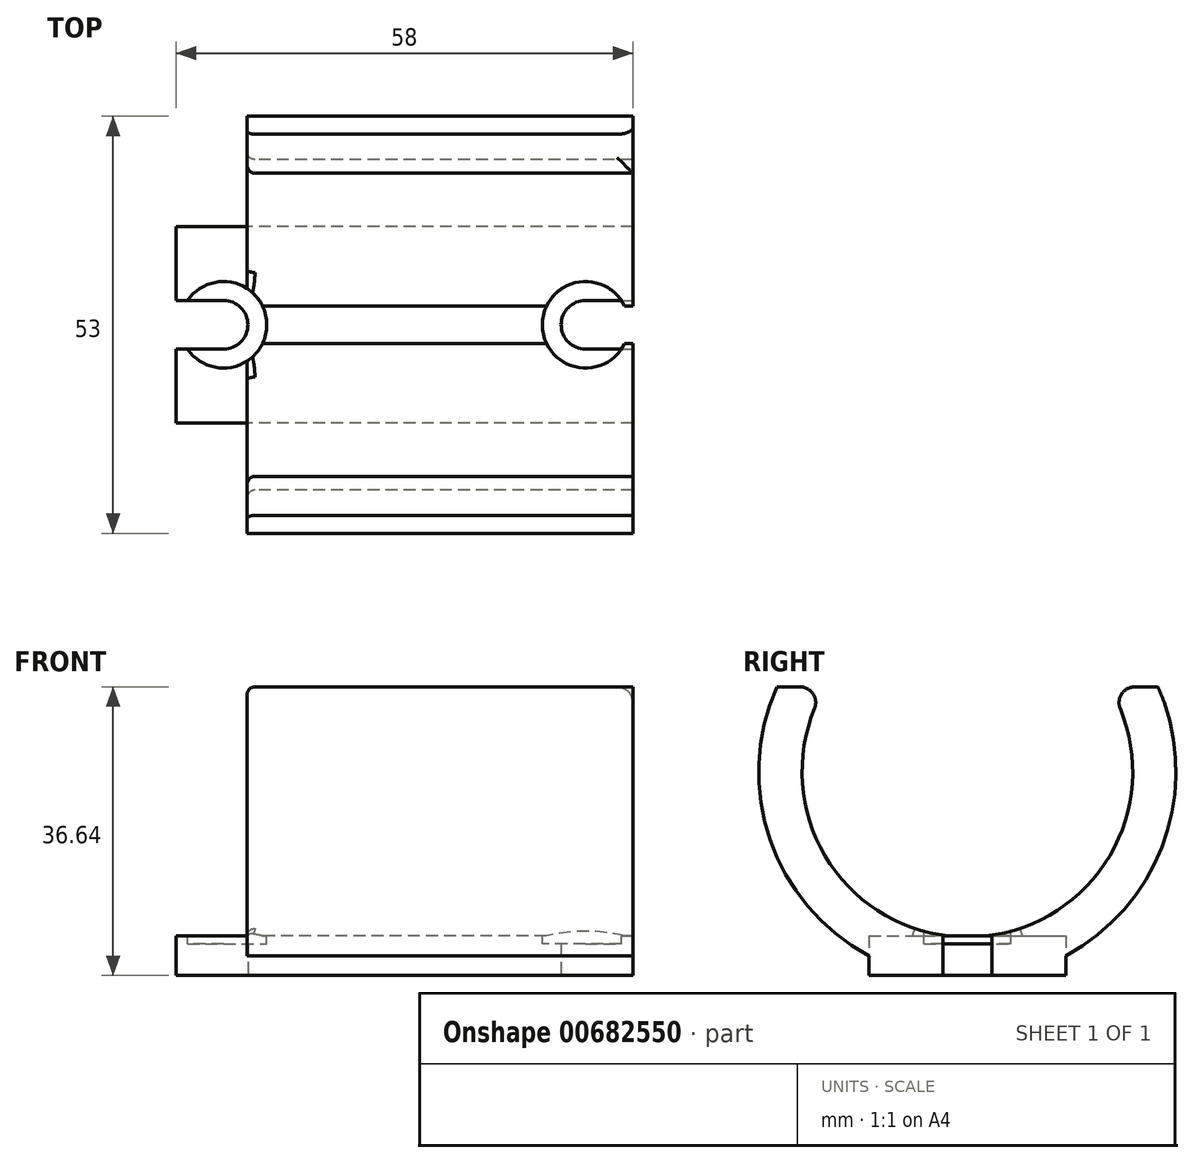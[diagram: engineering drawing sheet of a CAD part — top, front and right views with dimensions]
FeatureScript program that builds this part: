
annotation { "Feature Type Name" : "Feature", "Feature Type Description" : "" }
export const myFeature = defineFeature(function(context is Context, id is Id, definition is map)
    precondition{}
    {
        {
            var Q0;
            Q0=qCreatedBy(makeId("Top.planeOp"),FACE);
            var sketch = newSketch(context, id + "F0", { "sketchPlane" : qUnion([Q0])});
            skLineSegment(sketch, "E0.bottom", {"start": v(29, -12.5) * mm, "end": v(-29, -12.5) * mm});
            skLineSegment(sketch, "E0.top", {"start": v(29, 12.5) * mm, "end": v(-29, 12.5) * mm});
            skLineSegment(sketch, "E0.left", {"start": v(29, -12.5) * mm, "end": v(29, -3.1) * mm});
            skLineSegment(sketch, "E0.right", {"start": v(-29, -12.5) * mm, "end": v(-29, -3.1) * mm});
            skPoint(sketch, "E0.middle", {"position": v(0, 0) * mm});
            skArc(sketch, "E1", {"start": v(-23, -3.1) * mm, "mid": v(-19.9, 0) * mm, "end": v(-23, 3.1) * mm});
            skLineSegment(sketch, "E2", {"start": v(-23, -3.1) * mm, "end": v(-29, -3.1) * mm});
            skLineSegment(sketch, "E3", {"start": v(-23, 3.1) * mm, "end": v(-29, 3.1) * mm});
            skLineSegment(sketch, "E4.trimOffspring", {"start": v(-29, 3.1) * mm, "end": v(-29, 12.5) * mm});
            skLineSegment(sketch, "E5", {"start": v(0, 12.5) * mm, "end": v(0, -12.5) * mm, "construction": true});
            skLineSegment(sketch, "E6.MirrorCS", {"start": v(23, 3.1) * mm, "end": v(29, 3.1) * mm});
            skArc(sketch, "E7.MirrorCS", {"start": v(23, -3.1) * mm, "mid": v(19.9, 0) * mm, "end": v(23, 3.1) * mm});
            skLineSegment(sketch, "E8.MirrorCS", {"start": v(23, -3.1) * mm, "end": v(29, -3.1) * mm});
            skLineSegment(sketch, "E9.trimOffspring", {"start": v(29, 3.1) * mm, "end": v(29, 12.5) * mm});
            skSolve(sketch);
        }
        {
            var Q0;
            Q0 = qSketchRegion(id + "F0", true);
            extrude(context, id + "F1", {"entities" : qUnion([Q0]), "depth" : 5 * mm, "offsetDistance" : 25 * mm});
        }
        {
            var Q0;
            Q0=qCreatedBy(makeId("Right.planeOp"),FACE);
            var sketch = newSketch(context, id + "F2", { "sketchPlane" : qUnion([Q0])});
            skArc(sketch, "E10", {"start": v(-24.21, 36.64) * mm, "mid": v(-25.07, 17.27) * mm, "end": v(-12.5, 2.5) * mm});
            skArc(sketch, "E11", {"start": v(-18.02, 36.64) * mm, "mid": v(-18.82, 16.55) * mm, "end": v(-2.36, 5) * mm});
            skLineSegment(sketch, "E12", {"start": v(-24.21, 36.64) * mm, "end": v(-18.02, 36.64) * mm});
            skLineSegment(sketch, "E13.trimOffspring", {"start": v(18.02, 36.64) * mm, "end": v(24.21, 36.64) * mm});
            skLineSegment(sketch, "E14.0", {"start": v(-12.5, 5) * mm, "end": v(-2.36, 5) * mm});
            skLineSegment(sketch, "E15.0", {"start": v(-12.5, 5) * mm, "end": v(-12.5, 2.5) * mm});
            skPoint(sketch, "E16.orphan", {"position": v(-12.5, 0) * mm});
            skPoint(sketch, "E17.orphan", {"position": v(-3.1, 5) * mm});
            skLineSegment(sketch, "E18.0", {"start": v(2.36, 5) * mm, "end": v(12.5, 5) * mm});
            skLineSegment(sketch, "E19.0", {"start": v(12.5, 5) * mm, "end": v(12.5, 2.5) * mm});
            skPoint(sketch, "E20.orphan", {"position": v(12.5, 0) * mm});
            skPoint(sketch, "E21.orphan", {"position": v(3.1, 5) * mm});
            skArc(sketch, "E22.trimOffspring", {"start": v(2.36, 5) * mm, "mid": v(18.82, 16.55) * mm, "end": v(18.02, 36.64) * mm});
            skArc(sketch, "E23.trimOffspring", {"start": v(12.5, 2.5) * mm, "mid": v(25.07, 17.27) * mm, "end": v(24.21, 36.64) * mm});
            skSolve(sketch);
        }
        {
            var Q0;
            Q0 = qSketchRegion(id + "F2", true);
            var Q1;
            Q1=makeQuery(id+"F1.opExtrude","SWEPT_FACE",FACE,{"disambiguationData":[OSD([sQuery(id+"F0.wireOp",EDGE,"E9.trimOffspring")])]});
            extrude(context, id + "F3", {"entities" : qUnion([Q0]), "operationType" : NewBodyOperationType.ADD, "endBound" : BoundingType.UP_TO_SURFACE, "depth" : 32.5 * mm, "endBoundEntityFace" : qUnion([Q1]), "offsetDistance" : 25 * mm});
        }
        {
            var Q0;
            Q0 = qSketchRegion(id + "F2", true);
            extrude(context, id + "F4", {"entities" : qUnion([Q0]), "operationType" : NewBodyOperationType.ADD, "oppositeDirection" : true, "depth" : 20 * mm, "offsetDistance" : 25 * mm});
        }
        {
            var Q0;
            {var subQ0=sQuery(id+"F2.wireOp",EDGE,"E12");var subQ1=sQuery(id+"F2.wireOp",EDGE,"E11");Q0=makeQuery(id+"F4.boolean.opBoolean","MERGE",EDGE,{"derivedFrom":[makeQuery(id+"F3.opExtrude","SWEPT_EDGE",EDGE,{"disambiguationData":[OSD([subQ1,subQ0])]}),makeQuery(id+"F4.opExtrude","SWEPT_EDGE",EDGE,{"disambiguationData":[OSD([subQ1,subQ0])]})]});}
            var Q1;
            {var subQ0=sQuery(id+"F2.wireOp",EDGE,"E22.trimOffspring");var subQ1=sQuery(id+"F2.wireOp",EDGE,"E13.trimOffspring");Q1=makeQuery(id+"F4.boolean.opBoolean","MERGE",EDGE,{"derivedFrom":[makeQuery(id+"F3.opExtrude","SWEPT_EDGE",EDGE,{"disambiguationData":[OSD([subQ1,subQ0])]}),makeQuery(id+"F4.opExtrude","SWEPT_EDGE",EDGE,{"disambiguationData":[OSD([subQ1,subQ0])]})]});}
            var Q2;
            Q2=makeQuery(id+"F3.opExtrude","CAP_EDGE",EDGE,{"disambiguationData":[OSD([sQuery(id+"F2.wireOp",EDGE,"E13.trimOffspring")])],"isStart":false});
            fillet(context, id + "F5", {"entities" : qUnion([Q0, Q1, Q2]), "radius" : 2 * mm, "tangentPropagation" : true, "allowEdgeOverflow" : false});
        }
        {
            var Q0;
            Q0=makeQuery(id+"F1.opExtrude","CAP_FACE",FACE,{"disambiguationData":[OSD([sQuery(id+"F0.wireOp",EDGE,"E0.bottom"),sQuery(id+"F0.wireOp",EDGE,"E0.top"),sQuery(id+"F0.wireOp",EDGE,"E0.left"),sQuery(id+"F0.wireOp",EDGE,"E0.right"),sQuery(id+"F0.wireOp",EDGE,"E1"),sQuery(id+"F0.wireOp",EDGE,"E2"),sQuery(id+"F0.wireOp",EDGE,"E3"),sQuery(id+"F0.wireOp",EDGE,"E4.trimOffspring"),sQuery(id+"F0.wireOp",EDGE,"E6.MirrorCS"),sQuery(id+"F0.wireOp",EDGE,"E7.MirrorCS"),sQuery(id+"F0.wireOp",EDGE,"E8.MirrorCS"),sQuery(id+"F0.wireOp",EDGE,"E9.trimOffspring")])],"isStart":false});
            var sketch = newSketch(context, id + "F6", { "sketchPlane" : qUnion([Q0])});
            skCircle(sketch, "E24", {"center": v(-23, 0) * mm, "radius": 5.5 * mm});
            skCircle(sketch, "E25", {"center": v(23, 0) * mm, "radius": 5.5 * mm});
            skSolve(sketch);
        }
        {
            var Q0;
            Q0 = qSketchRegion(id + "F6", true);
            extrude(context, id + "F7", {"entities" : qUnion([Q0]), "operationType" : NewBodyOperationType.REMOVE, "oppositeDirection" : true, "depth" : 2 * mm, "offsetDistance" : 25 * mm, "symmetric" : true});
        }
        {
            var Q0;
            Q0=makeQuery(id+"F3.opExtrude","TWEAK_EDGE",EDGE,{"derivedFrom":[makeQuery(id+"F1.opExtrude","SWEPT_FACE",FACE,{"disambiguationData":[OSD([sQuery(id+"F0.wireOp",EDGE,"E9.trimOffspring")])]}),makeQuery(id+"F2.imprint","IMPRINT",EDGE,{"derivedFrom":sQuery(id+"F2.wireOp",EDGE,"E22.trimOffspring")})]});
            var Q1;
            Q1=makeQuery(id+"F3.opExtrude","TWEAK_EDGE",EDGE,{"derivedFrom":[makeQuery(id+"F1.opExtrude","SWEPT_FACE",FACE,{"disambiguationData":[OSD([sQuery(id+"F0.wireOp",EDGE,"E9.trimOffspring")])]}),makeQuery(id+"F2.imprint","IMPRINT",EDGE,{"derivedFrom":sQuery(id+"F2.wireOp",EDGE,"E11")})]});
            var Q2;
            Q2=makeQuery(id+"F4.opExtrude","CAP_EDGE",EDGE,{"disambiguationData":[OSD([sQuery(id+"F2.wireOp",EDGE,"E22.trimOffspring")])],"isStart":false});
            var Q3;
            Q3=makeQuery(id+"F4.opExtrude","CAP_EDGE",EDGE,{"disambiguationData":[OSD([sQuery(id+"F2.wireOp",EDGE,"E11")])],"isStart":false});
            fillet(context, id + "F8", {"entities" : qUnion([Q0, Q1, Q2, Q3]), "radius" : 1 * mm, "tangentPropagation" : true, "allowEdgeOverflow" : false});
        }
    });
